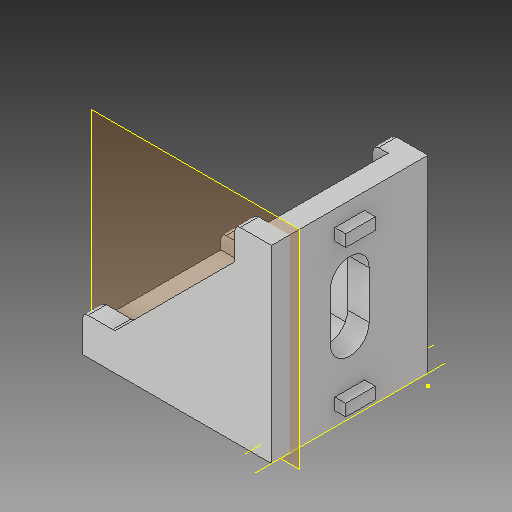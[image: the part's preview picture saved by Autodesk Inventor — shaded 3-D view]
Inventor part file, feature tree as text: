
AUTODESK INVENTOR PART (.ipt)
format: ipt  version: 2017 (Build 210142000, 142)  size: 179,712 bytes
history: native  units: mm
features: sketch x8, other x5, plane x1
ambient origin geometry x8: Origin, YZ Plane, XZ Plane, XY Plane, X Axis, Y Axis, Z Axis, Center Point
bodies: Solid1 (feature_tree)
feature tree (14):
  other  "30mm Bracket_CPY_MIR2_MIR1_MIR.ipt"
  other  "Solid1::30mm Bracket_CPY_MIR2_MIR1_MIR.ipt"
  other  "TaggingFeature1"
  sketch  "Sketch1"  dims[d0=10.0mm]
  sketch  "Sketch2"
  sketch  "Sketch3"
  sketch  "Sketch4"
  sketch  "Sketch5"
  sketch  "Sketch7"
  sketch  "Sketch9"
  sketch  "Sketch10"
  plane  "Work Plane1"
  other  "Work Axis1"
  other  "Work Axis2"
